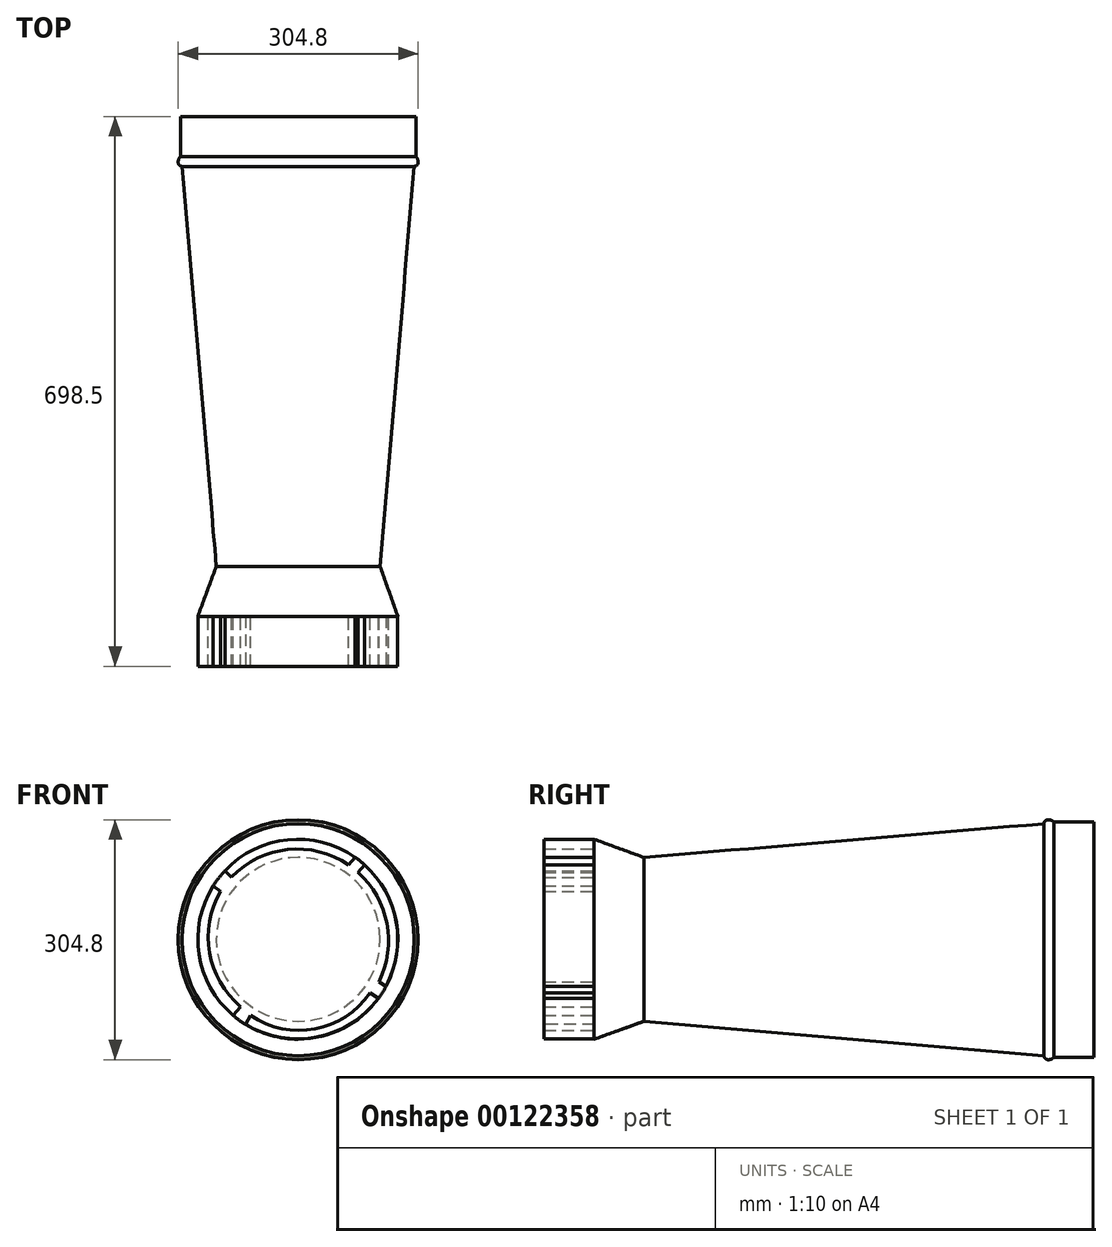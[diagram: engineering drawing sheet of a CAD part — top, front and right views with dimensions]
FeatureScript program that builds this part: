
annotation { "Feature Type Name" : "Feature", "Feature Type Description" : "" }
export const myFeature = defineFeature(function(context is Context, id is Id, definition is map)
    precondition{}
    {
        {
            var Q0;
            Q0=qCreatedBy(makeId("Front.planeOp"),FACE);
            var sketch = newSketch(context, id + "F0", { "sketchPlane" : qUnion([Q0])});
            skCircle(sketch, "E0", {"center": v(-292.87, -169.21) * mm, "radius": 149.42 * mm});
            skSolve(sketch);
        }
        {
            var Q0;
            Q0 = qSketchRegion(id + "F0", true);
            var Q1;
            Q1=makeQuery(id+"F0.imprint","IMPRINT",FACE,{"disambiguationData":[TD([[makeQuery(id+"F0.imprint","IMPRINT",EDGE,{"derivedFrom":sQuery(id+"F0.wireOp",EDGE,"E0")}),1.0]])]});
            extrude(context, id + "F1", {"entities" : qUnion([Q0, Q1]), "depth" : 50.8 * mm});
        }
        {
            var Q0;
            Q0=makeQuery(id+"F1.opExtrude","CAP_FACE",FACE,{"disambiguationData":[OSD([sQuery(id+"F0.wireOp",EDGE,"E0")])],"isStart":false});
            var sketch = newSketch(context, id + "F2", { "sketchPlane" : qUnion([Q0])});
            skCircle(sketch, "E1", {"center": v(-292.87, -169.21) * mm, "radius": 152.4 * mm});
            skSolve(sketch);
        }
        {
            var Q0;
            Q0=makeQuery(id+"F2.imprint","IMPRINT",FACE,{"disambiguationData":[TD([[makeQuery(id+"F2.imprint","IMPRINT",EDGE,{"derivedFrom":sQuery(id+"F2.wireOp",EDGE,"E1")}),1.0]])]});
            var Q1;
            Q1=makeQuery(id+"F2.imprint","IMPRINT",FACE,{"disambiguationData":[TD([[makeQuery(id+"F2.imprint","IMPRINT",EDGE,{"derivedFrom":makeQuery(id+"F1.opExtrude","CAP_EDGE",EDGE,{"disambiguationData":[OSD([sQuery(id+"F0.wireOp",EDGE,"E0")])],"isStart":false})}),1.0]])]});
            extrude(context, id + "F3", {"entities" : qUnion([Q0, Q1]), "operationType" : NewBodyOperationType.ADD, "depth" : 12.7 * mm});
        }
        {
            var Q0;
            Q0=makeQuery(id+"F3.opExtrude","CAP_EDGE",EDGE,{"disambiguationData":[OSD([sQuery(id+"F2.wireOp",EDGE,"E1")])],"isStart":true});
            fillet(context, id + "F4", {"entities" : qUnion([Q0]), "radius" : 10.16 * mm, "tangentPropagation" : true, "allowEdgeOverflow" : false});
        }
        {
            var Q0;
            Q0=makeQuery(id+"F3.opExtrude","CAP_EDGE",EDGE,{"disambiguationData":[OSD([sQuery(id+"F2.wireOp",EDGE,"E1")])],"isStart":false});
            fillet(context, id + "F5", {"entities" : qUnion([Q0]), "radius" : 5.08 * mm, "tangentPropagation" : true, "allowEdgeOverflow" : false});
        }
        {
            var Q0;
            Q0=makeQuery(id+"F3.opExtrude","CAP_FACE",FACE,{"disambiguationData":[OSD([sQuery(id+"F2.wireOp",EDGE,"E1")])],"isStart":false});
            cPlane(context, id + "F6", {"entities" : qUnion([Q0]), "cplaneType" : CPlaneType.OFFSET, "offset" : 508 * mm, "width" : 152.4 * mm, "height" : 152.4 * mm});
        }
        {
            var Q0;
            Q0=qCreatedBy(id+"F6.planeOp",FACE);
            var sketch = newSketch(context, id + "F7", { "sketchPlane" : qUnion([Q0])});
            skLineSegment(sketch, "E2.bottom", {"start": v(-470.66, 9) * mm, "end": v(-115.06, 9) * mm});
            skLineSegment(sketch, "E2.top", {"start": v(-470.66, -346.6) * mm, "end": v(-115.06, -346.6) * mm});
            skLineSegment(sketch, "E2.left", {"start": v(-470.66, 9) * mm, "end": v(-470.66, -346.6) * mm});
            skLineSegment(sketch, "E2.right", {"start": v(-115.06, 9) * mm, "end": v(-115.06, -346.6) * mm});
            skLineSegment(sketch, "E3", {"start": v(-292.86, 9) * mm, "end": v(-292.86, -64.79) * mm});
            skLineSegment(sketch, "E4", {"start": v(-470.66, -168.8) * mm, "end": v(-396.88, -168.8) * mm});
            skCircle(sketch, "E5", {"center": v(-292.86, -168.8) * mm, "radius": 104.02 * mm});
            skLineSegment(sketch, "E6.trimOffspring", {"start": v(-188.84, -168.8) * mm, "end": v(-115.06, -168.8) * mm});
            skLineSegment(sketch, "E7.trimOffspring", {"start": v(-292.86, -272.82) * mm, "end": v(-292.86, -346.6) * mm});
            skSolve(sketch);
        }
        {
            var Q0;
            Q0=makeQuery(id+"F3.opExtrude","CAP_FACE",FACE,{"disambiguationData":[OSD([sQuery(id+"F2.wireOp",EDGE,"E1")])],"isStart":false});
            var Q1;
            {var subQ0=sQuery(id+"F7.wireOp",EDGE,"E5");var subQ1=makeQuery(id+"F7.imprint","INTERSECT",VERTEX,{"derivedFrom":[sQuery(id+"F7.wireOp",EDGE,"E3"),subQ0]});Q1=makeQuery(id+"F7.imprint","IMPRINT",FACE,{"disambiguationData":[TD([[makeQuery(id+"F7.imprint","IMPRINT",EDGE,{"disambiguationData":[TD([[subQ1,1.0]])],"derivedFrom":subQ0}),1.0]])]});}
            loft(context, id + "F8", {"sheetProfilesArray" : [{ "sheetProfileEntities" : qUnion([Q0]) }, { "sheetProfileEntities" : qUnion([Q1]) }]});
        }
        {
            var Q0;
            {var subQ0=sQuery(id+"F7.wireOp",EDGE,"E5");var subQ1=makeQuery(id+"F7.imprint","INTERSECT",VERTEX,{"derivedFrom":[sQuery(id+"F7.wireOp",EDGE,"E3"),subQ0]});Q0=makeQuery(id+"F8.opLoft","CAP_FACE",FACE,{"disambiguationData":[OSD([makeQuery(id+"F7.imprint","IMPRINT",FACE,{"disambiguationData":[TD([[makeQuery(id+"F7.imprint","IMPRINT",EDGE,{"disambiguationData":[TD([[subQ1,1.0]])],"derivedFrom":subQ0}),1.0]])]})])],"isStart":true});}
            cPlane(context, id + "F9", {"entities" : qUnion([Q0]), "cplaneType" : CPlaneType.OFFSET, "offset" : 63.5 * mm, "width" : 152.4 * mm, "height" : 152.4 * mm});
        }
        {
            var Q0;
            Q0=qCreatedBy(id+"F9.planeOp",FACE);
            var sketch = newSketch(context, id + "F10", { "sketchPlane" : qUnion([Q0])});
            skCircle(sketch, "E8", {"center": v(-293.3, -168.61) * mm, "radius": 127 * mm});
            skPoint(sketch, "E8.first.point", {"position": v(-385.95, -81.76) * mm});
            skPoint(sketch, "E8.second.point", {"position": v(-194.45, -248.35) * mm});
            skPoint(sketch, "E8.third.point", {"position": v(-177.28, -116.96) * mm});
            skSolve(sketch);
        }
        {
            var Q1;
            {var subQ0=sQuery(id+"F7.wireOp",EDGE,"E5");var subQ1=makeQuery(id+"F7.imprint","INTERSECT",VERTEX,{"derivedFrom":[sQuery(id+"F7.wireOp",EDGE,"E3"),subQ0]});Q1=makeQuery(id+"F8.opLoft","CAP_FACE",FACE,{"disambiguationData":[OSD([makeQuery(id+"F7.imprint","IMPRINT",FACE,{"disambiguationData":[TD([[makeQuery(id+"F7.imprint","IMPRINT",EDGE,{"disambiguationData":[TD([[subQ1,1.0]])],"derivedFrom":subQ0}),1.0]])]})])],"isStart":true});}
            var Q2;
            Q2=makeQuery(id+"F10.imprint","IMPRINT",FACE,{"disambiguationData":[TD([[makeQuery(id+"F10.imprint","IMPRINT",EDGE,{"derivedFrom":sQuery(id+"F10.wireOp",EDGE,"E8")}),1.0]])]});
            loft(context, id + "F11", {"operationType" : NewBodyOperationType.ADD, "sheetProfilesArray" : [{ "sheetProfileEntities" : qUnion([Q1]) }, { "sheetProfileEntities" : qUnion([Q2]) }]});
        }
        {
            var Q0;
            Q0=makeQuery(id+"F11.opLoft","CAP_FACE",FACE,{"disambiguationData":[OSD([makeQuery(id+"F10.imprint","IMPRINT",FACE,{"disambiguationData":[TD([[makeQuery(id+"F10.imprint","IMPRINT",EDGE,{"derivedFrom":sQuery(id+"F10.wireOp",EDGE,"E8")}),1.0]])]})])],"isStart":true});
            var sketch = newSketch(context, id + "F12", { "sketchPlane" : qUnion([Q0])});
            skArc(sketch, "E9", {"start": v(-208.54, -74.03) * mm, "mid": v(-298.72, -41.73) * mm, "end": v(-385.8, -81.6) * mm});
            skLineSegment(sketch, "E10", {"start": v(-385.8, -81.6) * mm, "end": v(-377.6, -89.76) * mm});
            skLineSegment(sketch, "E11", {"start": v(-208.54, -74.03) * mm, "end": v(-216.76, -83.72) * mm});
            skArc(sketch, "E12", {"start": v(-216.76, -83.72) * mm, "mid": v(-298.4, -54.16) * mm, "end": v(-377.6, -89.76) * mm});
            skLineSegment(sketch, "E13", {"start": v(-208.54, -74.03) * mm, "end": v(-216.89, -83.6) * mm});
            skArc(sketch, "E14", {"start": v(-400.92, -101.19) * mm, "mid": v(-418.8, -188.03) * mm, "end": v(-375.52, -265.4) * mm});
            skLineSegment(sketch, "E15", {"start": v(-228.8, -74.25) * mm, "end": v(-220.4, -64.62) * mm});
            skLineSegment(sketch, "E16", {"start": v(-400.92, -101.19) * mm, "end": v(-391.6, -108) * mm});
            skArc(sketch, "E17", {"start": v(-391.6, -108) * mm, "mid": v(-405.4, -185.84) * mm, "end": v(-365.79, -254.25) * mm});
            skLineSegment(sketch, "E18.trimOffspring", {"start": v(-365.79, -254.25) * mm, "end": v(-375.52, -265.4) * mm});
            skArc(sketch, "E19", {"start": v(-190.42, -222.49) * mm, "mid": v(-180.29, -148.68) * mm, "end": v(-216.76, -83.72) * mm});
            skArc(sketch, "E20", {"start": v(-181.2, -228.3) * mm, "mid": v(-168.36, -146.47) * mm, "end": v(-208.54, -74.03) * mm});
            skLineSegment(sketch, "E21", {"start": v(-181.2, -228.3) * mm, "end": v(-190.42, -222.49) * mm});
            skArc(sketch, "E22", {"start": v(-360.02, -276.68) * mm, "mid": v(-269.19, -292.86) * mm, "end": v(-191, -243.88) * mm});
            skArc(sketch, "E23", {"start": v(-353.22, -265.5) * mm, "mid": v(-271.56, -282.63) * mm, "end": v(-201.67, -237.05) * mm});
            skLineSegment(sketch, "E24", {"start": v(-360.02, -276.68) * mm, "end": v(-353.22, -265.5) * mm});
            skLineSegment(sketch, "E25", {"start": v(-201.67, -237.05) * mm, "end": v(-191, -243.88) * mm});
            skSolve(sketch);
        }
        {
            var Q0;
            {var subQ0=sQuery(id+"F12.wireOp",EDGE,"E16");Q0=makeQuery(id+"F12.imprint","IMPRINT",FACE,{"disambiguationData":[TD([[makeQuery(id+"F12.imprint","IMPRINT",EDGE,{"derivedFrom":subQ0}),-1.0]])]});}
            var Q1;
            {var subQ1=sQuery(id+"F12.wireOp",EDGE,"E10");Q1=makeQuery(id+"F12.imprint","IMPRINT",FACE,{"disambiguationData":[TD([[makeQuery(id+"F12.imprint","IMPRINT",EDGE,{"derivedFrom":subQ1}),1.0]])]});}
            var Q2;
            Q2=makeQuery(id+"F12.imprint","IMPRINT",FACE,{"disambiguationData":[TD([[makeQuery(id+"F12.imprint","IMPRINT",EDGE,{"derivedFrom":sQuery(id+"F12.wireOp",EDGE,"E22")}),1.0]])]});
            var Q3;
            {var subQ0=sQuery(id+"F12.wireOp",EDGE,"E11");Q3=makeQuery(id+"F12.imprint","IMPRINT",FACE,{"disambiguationData":[TD([[makeQuery(id+"F12.imprint","IMPRINT",EDGE,{"derivedFrom":subQ0}),-1.0]])]});}
            var Q4;
            Q4=makeQuery(id+"F12.imprint","IMPRINT",FACE,{"disambiguationData":[TD([[makeQuery(id+"F12.imprint","IMPRINT",EDGE,{"derivedFrom":sQuery(id+"F12.wireOp",EDGE,"E11")}),1.0]])]});
            extrude(context, id + "F13", {"entities" : qUnion([Q0, Q1, Q2, Q3, Q4]), "operationType" : NewBodyOperationType.ADD, "depth" : 63.5 * mm});
        }
    });
